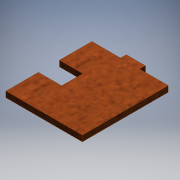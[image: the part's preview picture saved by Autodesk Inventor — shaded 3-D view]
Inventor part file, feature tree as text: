
AUTODESK INVENTOR PART (.ipt)
format: ipt  version: 2016 (Build 200138000, 138)  size: 128,512 bytes
history: native  units: mm
features: extrude x2, sketch x2, other x1, projected_geometry x1
ambient origin geometry x8: Origin, YZ Plane, XZ Plane, XY Plane, X Axis, Y Axis, Z Axis, Center Point
bodies: Body1 (feature_tree)
feature tree (6):
  other  "Sólido1"
  extrude  "Extrusión1"  Depth=3.0mm TaperAngle=0.0deg
  extrude  "Extrusión2"  [1 undecoded]
  sketch  "Boceto1"  dims[d0=3.0mm d1=0.0mm d2=3.0mm d3=0.0mm]
  sketch  "Boceto2"
  projected_geometry  "Contorno proyectado1"
note: 1 required parameter value undecoded (feature->parameter linkage not recoverable at this tier; creation-order binding heuristic only, values carry confidence <= 0.55)
